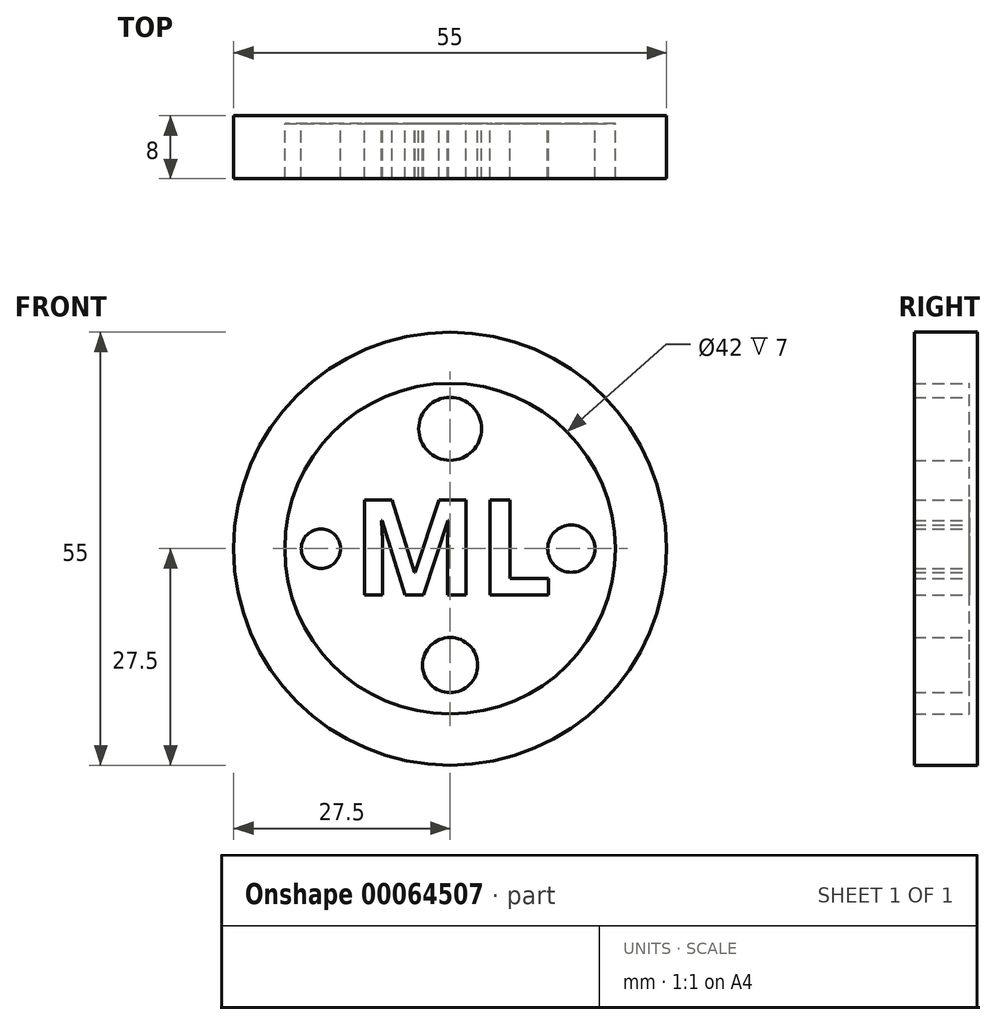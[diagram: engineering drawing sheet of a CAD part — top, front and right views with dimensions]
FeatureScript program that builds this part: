
annotation { "Feature Type Name" : "Feature", "Feature Type Description" : "" }
export const myFeature = defineFeature(function(context is Context, id is Id, definition is map)
    precondition{}
    {
        {
            var Q0;
            Q0=qCreatedBy(makeId("Front.planeOp"),FACE);
            var sketch = newSketch(context, id + "F0", { "sketchPlane" : qUnion([Q0])});
            skCircle(sketch, "E0", {"center": v(0, 0) * mm, "radius": 27.5 * mm});
            skCircle(sketch, "E1", {"center": v(0, 0) * mm, "radius": 21 * mm});
            skSolve(sketch);
        }
        {
            var Q0;
            Q0 = qSketchRegion(id + "F0", true);
            extrude(context, id + "F1", {"entities" : qUnion([Q0]), "depth" : 8 * mm});
        }
        {
            var Q0;
            Q0=qCreatedBy(makeId("Front.planeOp"),FACE);
            var sketch = newSketch(context, id + "F2", { "sketchPlane" : qUnion([Q0])});
            skCircle(sketch, "E2", {"center": v(0, 0) * mm, "radius": 27.24 * mm});
            skSolve(sketch);
        }
        {
            var Q0;
            Q0 = qSketchRegion(id + "F2", true);
            extrude(context, id + "F3", {"entities" : qUnion([Q0]), "operationType" : NewBodyOperationType.ADD, "depth" : 1 * mm});
        }
        {
            var Q0;
            Q0=qCreatedBy(makeId("Front.planeOp"),FACE);
            var sketch = newSketch(context, id + "F4", { "sketchPlane" : qUnion([Q0])});
            skText(sketch, "E3", { "text": "ML", "fontName": "OpenSans-Bold.ttf"});
            const initialGuessF4  = {"E3": [-0.01236, -0.00587, 1, 0, 0.01215]};
            skSetInitialGuess(sketch, initialGuessF4);
            skSolve(sketch);
        }
        {
            var Q0;
            Q0 = qSketchRegion(id + "F4", true);
            extrude(context, id + "F5", {"entities" : qUnion([Q0]), "operationType" : NewBodyOperationType.ADD, "depth" : 8 * mm});
        }
        {
            var Q0;
            Q0=qCreatedBy(makeId("Front.planeOp"),FACE);
            var sketch = newSketch(context, id + "F6", { "sketchPlane" : qUnion([Q0])});
            skCircle(sketch, "E4", {"center": v(0, 15.23) * mm, "radius": 4 * mm});
            skCircle(sketch, "E5", {"center": v(0, -14.79) * mm, "radius": 3.5 * mm});
            skCircle(sketch, "E6", {"center": v(15.4, 0) * mm, "radius": 3 * mm});
            skCircle(sketch, "E7", {"center": v(-16.4, 0) * mm, "radius": 2.5 * mm});
            skSolve(sketch);
        }
        {
            var Q0;
            Q0 = qSketchRegion(id + "F6", true);
            extrude(context, id + "F7", {"entities" : qUnion([Q0]), "operationType" : NewBodyOperationType.ADD, "depth" : 8 * mm});
        }
    });
